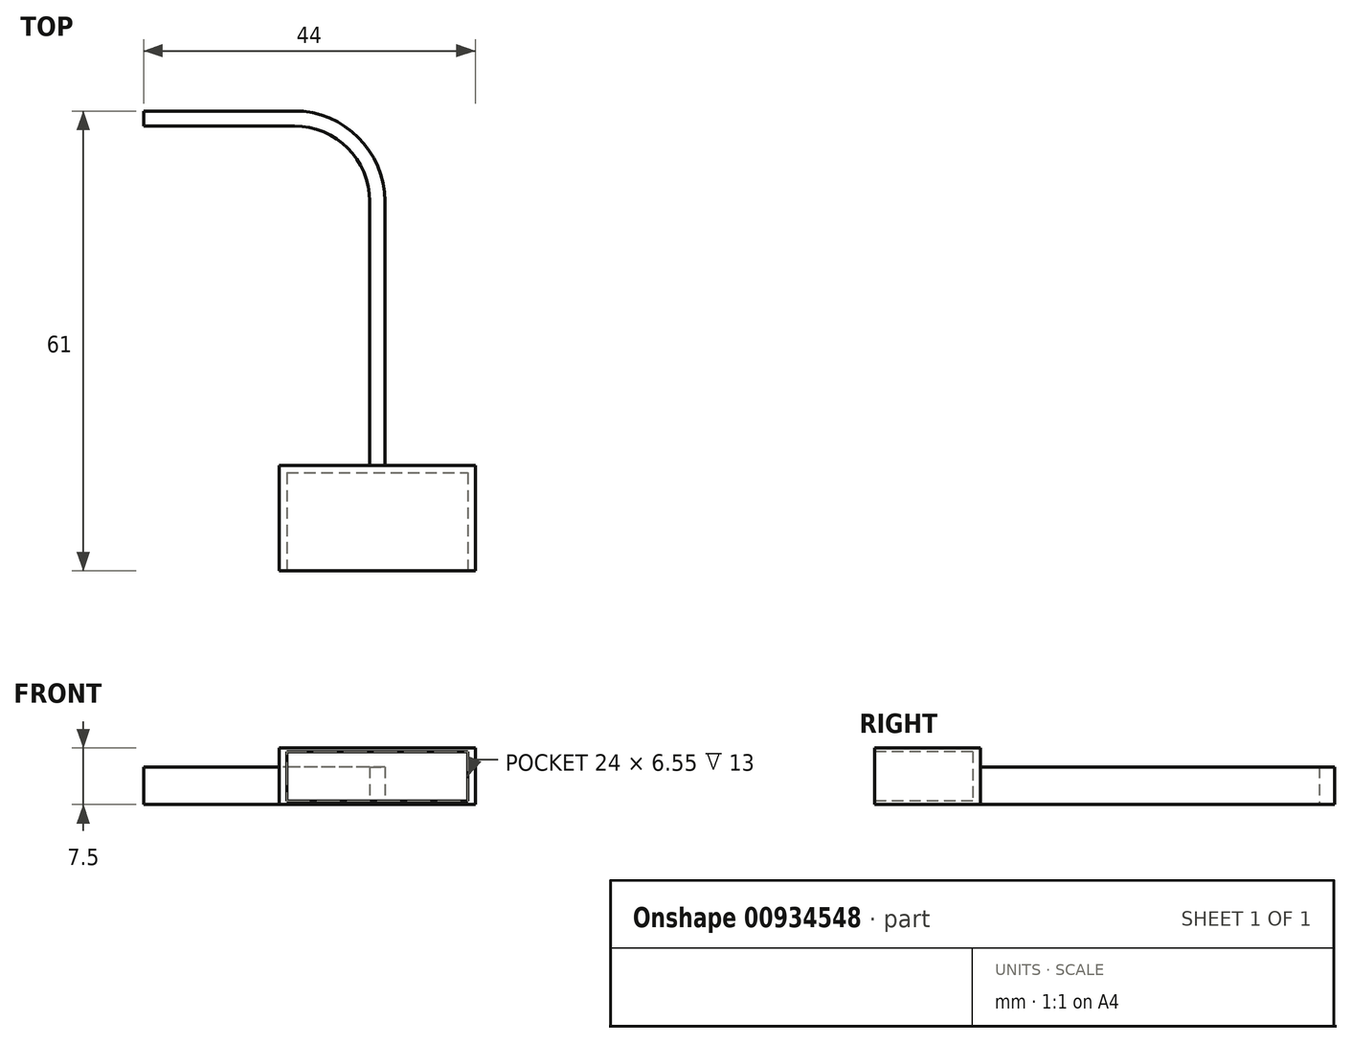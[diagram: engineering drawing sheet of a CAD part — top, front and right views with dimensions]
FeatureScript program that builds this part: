
annotation { "Feature Type Name" : "Feature", "Feature Type Description" : "" }
export const myFeature = defineFeature(function(context is Context, id is Id, definition is map)
    precondition{}
    {
        {
            var Q0;
            Q0=qCreatedBy(makeId("Top.planeOp"),FACE);
            var sketch = newSketch(context, id + "F0", { "sketchPlane" : qUnion([Q0])});
            skLineSegment(sketch, "E0.bottom", {"start": v(-5, 5) * mm, "end": v(5, 5) * mm});
            skLineSegment(sketch, "E0.top", {"start": v(-5, -5) * mm, "end": v(5, -5) * mm});
            skLineSegment(sketch, "E0.left", {"start": v(-5, 5) * mm, "end": v(-5, -5) * mm});
            skLineSegment(sketch, "E0.right", {"start": v(5, 5) * mm, "end": v(5, -5) * mm});
            skPoint(sketch, "E0.middle", {"position": v(0, 0) * mm});
            skArc(sketch, "E1", {"start": v(5, -5) * mm, "mid": v(2.07, 2.07) * mm, "end": v(-5, 5) * mm});
            skLineSegment(sketch, "E2", {"start": v(5, -5) * mm, "end": v(5, -40) * mm});
            skLineSegment(sketch, "E3", {"start": v(-5, 5) * mm, "end": v(-25, 5) * mm});
            skLineSegment(sketch, "E4.0", {"start": v(-5, 7) * mm, "end": v(-25, 7) * mm});
            skArc(sketch, "E5.0", {"start": v(7, -5) * mm, "mid": v(3.49, 3.49) * mm, "end": v(-5, 7) * mm});
            skLineSegment(sketch, "E6.0", {"start": v(7, -5) * mm, "end": v(7, -40) * mm});
            skLineSegment(sketch, "E7", {"start": v(-25, 7) * mm, "end": v(-25, 5) * mm});
            skLineSegment(sketch, "E8", {"start": v(5, -40) * mm, "end": v(7, -40) * mm});
            skLineSegment(sketch, "E9.bottom", {"start": v(6, -40) * mm, "end": v(19, -40) * mm});
            skLineSegment(sketch, "E9.top", {"start": v(6, -54) * mm, "end": v(19, -54) * mm});
            skLineSegment(sketch, "E9.left", {"start": v(6, -40) * mm, "end": v(6, -54) * mm});
            skLineSegment(sketch, "E9.right", {"start": v(19, -40) * mm, "end": v(19, -54) * mm});
            skLineSegment(sketch, "E10.MirrorCS", {"start": v(6, -40) * mm, "end": v(-7, -40) * mm});
            skLineSegment(sketch, "E11.MirrorCS", {"start": v(-7, -40) * mm, "end": v(-7, -54) * mm});
            skLineSegment(sketch, "E12.MirrorCS", {"start": v(6, -54) * mm, "end": v(-7, -54) * mm});
            skLineSegment(sketch, "E13.0", {"start": v(19, -5) * mm, "end": v(19, -40) * mm});
            skArc(sketch, "E14.0", {"start": v(19, -5) * mm, "mid": v(11.97, 11.97) * mm, "end": v(-5, 19) * mm});
            skLineSegment(sketch, "E15.0", {"start": v(-5, 19) * mm, "end": v(-25, 19) * mm});
            skLineSegment(sketch, "E16.MirrorCS", {"start": v(-7, -5) * mm, "end": v(-7, -40) * mm});
            skLineSegment(sketch, "E17", {"start": v(-25, 6) * mm, "end": v(-5, 6) * mm});
            skLineSegment(sketch, "E18.MirrorCS", {"start": v(-5, -7) * mm, "end": v(-25, -7) * mm});
            skArc(sketch, "E19", {"start": v(-6.95, -17.1) * mm, "mid": v(-9.88, -10.02) * mm, "end": v(-16.95, -7.1) * mm});
            skSolve(sketch);
        }
        {
            var Q0;
            {var subQ4=sQuery(id+"F0.wireOp",EDGE,"E3");Q0=makeQuery(id+"F0.imprint","IMPRINT",FACE,{"disambiguationData":[TD([[makeQuery(id+"F0.imprint","IMPRINT",EDGE,{"derivedFrom":subQ4}),-1.0]])]});}
            var Q1;
            {var subQ0=sQuery(id+"F0.wireOp",EDGE,"E1");Q1=makeQuery(id+"F0.imprint","IMPRINT",FACE,{"disambiguationData":[TD([[makeQuery(id+"F0.imprint","IMPRINT",EDGE,{"derivedFrom":subQ0}),-1.0]])]});}
            var Q2;
            {var subQ1=sQuery(id+"F0.wireOp",EDGE,"E2");Q2=makeQuery(id+"F0.imprint","IMPRINT",FACE,{"disambiguationData":[TD([[makeQuery(id+"F0.imprint","IMPRINT",EDGE,{"derivedFrom":subQ1}),1.0]])]});}
            extrude(context, id + "F1", {"entities" : qUnion([Q0, Q1, Q2]), "depth" : 5 * mm, "offsetDistance" : 25 * mm});
        }
        {
            var Q0;
            {var subQ3=sQuery(id+"F0.wireOp",EDGE,"E9.left");Q0=makeQuery(id+"F0.imprint","IMPRINT",FACE,{"disambiguationData":[TD([[makeQuery(id+"F0.imprint","IMPRINT",EDGE,{"derivedFrom":subQ3}),-1.0]])]});}
            var Q1;
            Q1=makeQuery(id+"F0.imprint","IMPRINT",FACE,{"disambiguationData":[TD([[makeQuery(id+"F0.imprint","IMPRINT",EDGE,{"derivedFrom":sQuery(id+"F0.wireOp",EDGE,"E9.top")}),1.0]])]});
            extrude(context, id + "F2", {"entities" : qUnion([Q0, Q1]), "operationType" : NewBodyOperationType.ADD, "depth" : 7.5 * mm, "offsetDistance" : 25 * mm});
        }
        {
            var Q0;
            Q0=makeQuery(id+"F2.opExtrude","SWEPT_FACE",FACE,{"disambiguationData":[OSD([sQuery(id+"F0.wireOp",EDGE,"E9.top"),sQuery(id+"F0.wireOp",EDGE,"E12.MirrorCS")])]});
            var sketch = newSketch(context, id + "F3", { "sketchPlane" : qUnion([Q0])});
            skLineSegment(sketch, "E20", {"start": v(6, 7.5) * mm, "end": v(6, 0) * mm});
            skLineSegment(sketch, "E21", {"start": v(-7, 3.75) * mm, "end": v(19, 3.75) * mm});
            skLineSegment(sketch, "E22.bottom", {"start": v(-6, 7.03) * mm, "end": v(18, 7.03) * mm});
            skLineSegment(sketch, "E22.top", {"start": v(-6, 0.47) * mm, "end": v(18, 0.47) * mm});
            skLineSegment(sketch, "E22.left", {"start": v(-6, 7.03) * mm, "end": v(-6, 0.47) * mm});
            skLineSegment(sketch, "E22.right", {"start": v(18, 7.03) * mm, "end": v(18, 0.47) * mm});
            skPoint(sketch, "E22.middle", {"position": v(6, 3.75) * mm});
            skSolve(sketch);
        }
        {
            var Q0;
            {var subQ0=sQuery(id+"F3.wireOp",EDGE,"E22.bottom");var subQ1=sQuery(id+"F3.wireOp",EDGE,"E20");var subQ2=makeQuery(id+"F3.imprint","INTERSECT",VERTEX,{"derivedFrom":[subQ1,subQ0]});Q0=makeQuery(id+"F3.imprint","IMPRINT",FACE,{"disambiguationData":[TD([[makeQuery(id+"F3.imprint","IMPRINT",EDGE,{"disambiguationData":[TD([[subQ2,-1.0]])],"derivedFrom":subQ1}),-1.0]])]});}
            var Q1;
            {var subQ0=sQuery(id+"F3.wireOp",EDGE,"E22.bottom");var subQ1=sQuery(id+"F3.wireOp",EDGE,"E20");var subQ2=makeQuery(id+"F3.imprint","INTERSECT",VERTEX,{"derivedFrom":[subQ1,subQ0]});Q1=makeQuery(id+"F3.imprint","IMPRINT",FACE,{"disambiguationData":[TD([[makeQuery(id+"F3.imprint","IMPRINT",EDGE,{"disambiguationData":[TD([[subQ2,-1.0]])],"derivedFrom":subQ1}),1.0]])]});}
            var Q2;
            {var subQ0=sQuery(id+"F3.wireOp",EDGE,"E21");var subQ1=sQuery(id+"F3.wireOp",EDGE,"E20");var subQ2=makeQuery(id+"F3.imprint","INTERSECT",VERTEX,{"derivedFrom":[subQ1,subQ0]});Q2=makeQuery(id+"F3.imprint","IMPRINT",FACE,{"disambiguationData":[TD([[makeQuery(id+"F3.imprint","IMPRINT",EDGE,{"disambiguationData":[TD([[subQ2,-1.0]])],"derivedFrom":subQ1}),1.0]])]});}
            var Q3;
            {var subQ0=sQuery(id+"F3.wireOp",EDGE,"E21");var subQ1=sQuery(id+"F3.wireOp",EDGE,"E20");var subQ2=makeQuery(id+"F3.imprint","INTERSECT",VERTEX,{"derivedFrom":[subQ1,subQ0]});Q3=makeQuery(id+"F3.imprint","IMPRINT",FACE,{"disambiguationData":[TD([[makeQuery(id+"F3.imprint","IMPRINT",EDGE,{"disambiguationData":[TD([[subQ2,-1.0]])],"derivedFrom":subQ1}),-1.0]])]});}
            extrude(context, id + "F4", {"entities" : qUnion([Q0, Q1, Q2, Q3]), "operationType" : NewBodyOperationType.REMOVE, "oppositeDirection" : true, "depth" : 13 * mm, "offsetDistance" : 25 * mm});
        }
    });
